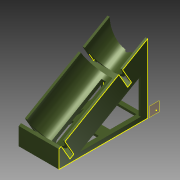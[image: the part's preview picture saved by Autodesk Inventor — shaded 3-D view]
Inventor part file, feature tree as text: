
AUTODESK INVENTOR PART (.ipt)
format: ipt  version: 2013 (Build 170138000, 138)  size: 432,640 bytes
history: native  units: mm
features: sketch x29, extrude x27, other x2
ambient origin geometry x8: Origin, YZ Plane, XZ Plane, XY Plane, X Axis, Y Axis, Z Axis, Center Point
feature tree (58):
  other  "ソリッド1"
  extrude  "押し出し1"  Depth=200.0mm
  extrude  "押し出し2"  TaperAngle=30.0deg  [1 undecoded]
  extrude  "押し出し3"  Depth=80.0mm TaperAngle=0.0deg
  extrude  "押し出し4"  Depth=40.0mm TaperAngle=0.0deg
  extrude  "押し出し5"  Depth=220.0mm TaperAngle=0.0deg
  extrude  "押し出し6"  Depth=5.0mm TaperAngle=0.0deg
  extrude  "押し出し7"  Depth=5.0mm TaperAngle=0.0deg
  extrude  "押し出し8"  Depth=5.0mm TaperAngle=0.0deg
  extrude  "押し出し9"  Depth=225.0mm
  sketch  "スケッチ10"
  other  "作業平面2"
  extrude  "押し出し10"  Depth=10.0mm
  extrude  "押し出し11"  Depth=140.0mm
  extrude  "押し出し12"  Depth=10.0mm
  extrude  "押し出し13"  Depth=90.0mm TaperAngle=0.0deg
  extrude  "押し出し14"  Depth=90.0mm TaperAngle=0.0deg
  extrude  "押し出し15"  Depth=200.0mm
  extrude  "押し出し16"  Depth=90.0mm TaperAngle=0.0deg
  extrude  "押し出し17"  TaperAngle=30.0deg  [1 undecoded]
  sketch  "スケッチ19"
  extrude  "押し出し18"  Depth=80.0mm TaperAngle=0.0deg
  extrude  "押し出し19"  Depth=7.0mm TaperAngle=0.0deg
  extrude  "押し出し20"  Depth=60.0mm
  extrude  "押し出し21"  Depth=15.0mm
  extrude  "押し出し22"  Depth=10.0mm
  extrude  "押し出し23"  Depth=15.0mm
  extrude  "押し出し24"  Depth=15.0mm
  extrude  "押し出し26"  Depth=25.0mm
  extrude  "押し出し27"  Depth=7.0mm TaperAngle=0.0deg
  extrude  "押し出し28"  Depth=5.0mm
  sketch  "スケッチ1"
  sketch  "スケッチ2"
  sketch  "スケッチ3"
  sketch  "スケッチ4"
  sketch  "スケッチ5"
  sketch  "スケッチ6"
  sketch  "スケッチ7"
  sketch  "スケッチ8"
  sketch  "スケッチ9"
  sketch  "スケッチ11"
  sketch  "スケッチ12"
  sketch  "スケッチ13"
  sketch  "スケッチ14"
  sketch  "スケッチ15"
  sketch  "スケッチ16"
  sketch  "スケッチ17"
  sketch  "スケッチ18"
  sketch  "スケッチ20"
  sketch  "スケッチ21"
  sketch  "スケッチ22"
  sketch  "スケッチ23"
  sketch  "スケッチ24"
  sketch  "スケッチ25"
  sketch  "スケッチ26"
  sketch  "スケッチ27"
  sketch  "スケッチ28"
  sketch  "スケッチ29"
note: 2 required parameter values undecoded (feature->parameter linkage not recoverable at this tier; creation-order binding heuristic only, values carry confidence <= 0.55)
